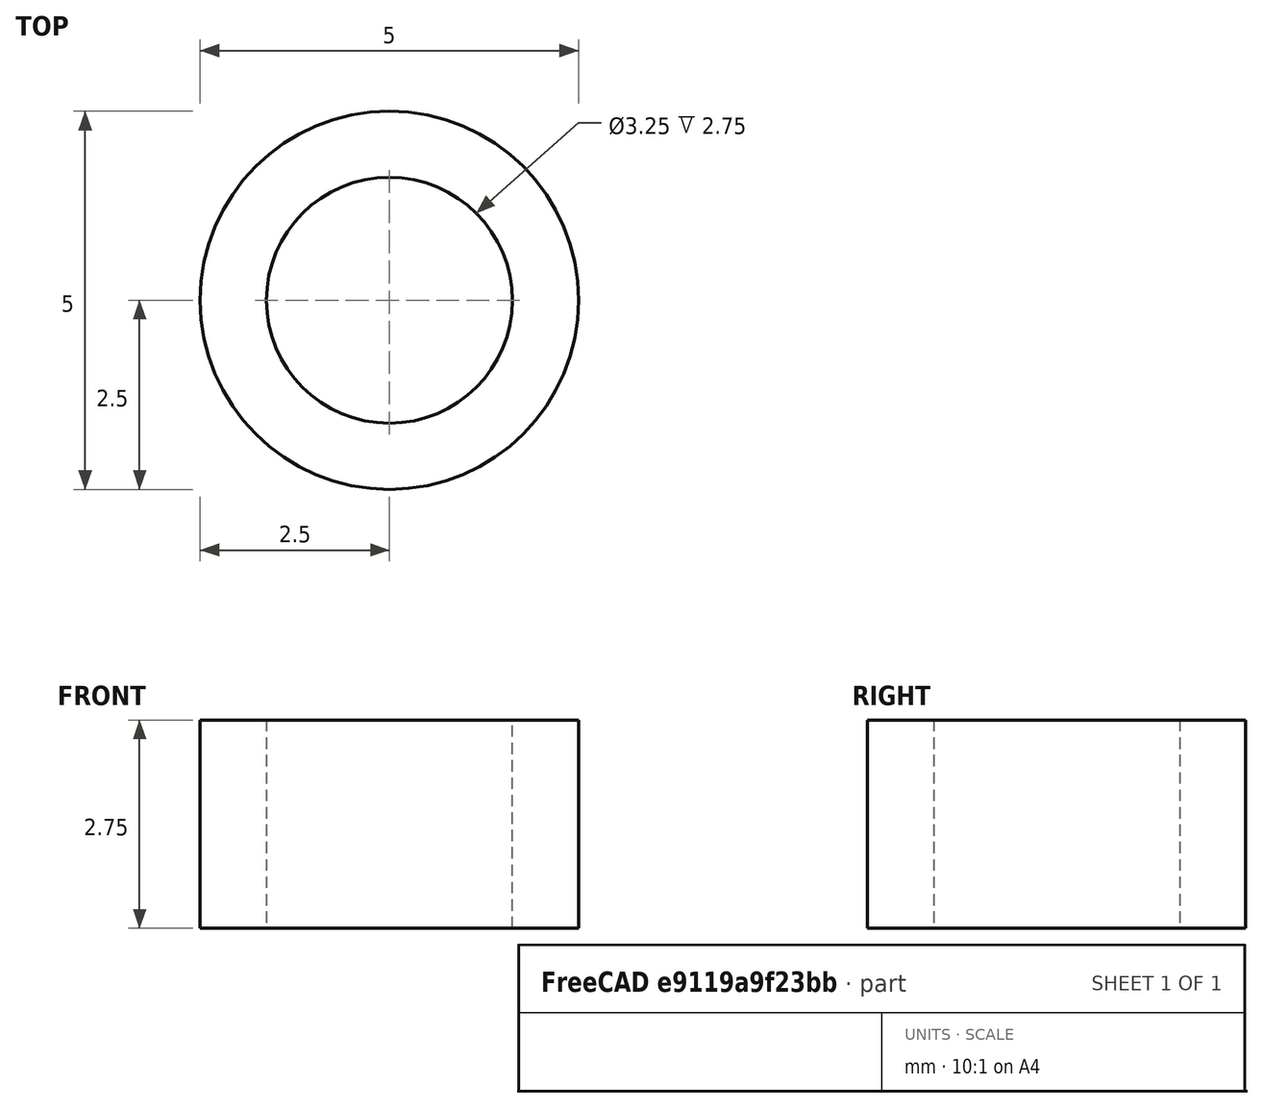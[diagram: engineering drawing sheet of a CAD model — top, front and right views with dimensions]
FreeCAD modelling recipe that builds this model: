
FCSTD DOCUMENT  (FreeCAD 0.20R29177 +233 (Git))
Label: scroll_wheel_spacer
License: All rights reserved
LicenseURL: http://en.wikipedia.org/wiki/All_rights_reserved
objects: Sketcher::SketchObject×1, PartDesign::Pad×1, PartDesign::Body×1
note: 4 computed .brp shape members not serialized (recipe doc carries the construction recipe); baked Part::Feature solids carry a one-line shape summary decoded from their .brp

FEATURE [Sketcher::SketchObject] Sketch
  FullyConstrained = true
  MapMode = 5
  Support = -> [XY_Plane]
  sketch-geometry (2):
    g0: Circle CenterX=0 CenterY=0 CenterZ=0 NormalX=0 NormalY=0 NormalZ=1 AngleXU=0 Radius=1.625
    g1: Circle CenterX=0 CenterY=0 CenterZ=0 NormalX=0 NormalY=0 NormalZ=1 AngleXU=0 Radius=2.5
  constraints (4):
    c: Coincident(g0,g-1)
    c: Coincident(g1,g0)
    c: Diameter(g0) = 3.25
    c: Diameter(g1) = 5
FEATURE [PartDesign::Pad] Pad
  Direction = (0,0,1)
  Length = 2.75
  Length2 = 10
  Profile = -> Sketch
  ReferenceAxis = -> Sketch [N_Axis]
  Type = 0
FEATURE [PartDesign::Body] Body
  Group = -> [Sketch,Pad]
  Origin = -> Origin
  Tip = -> Pad
